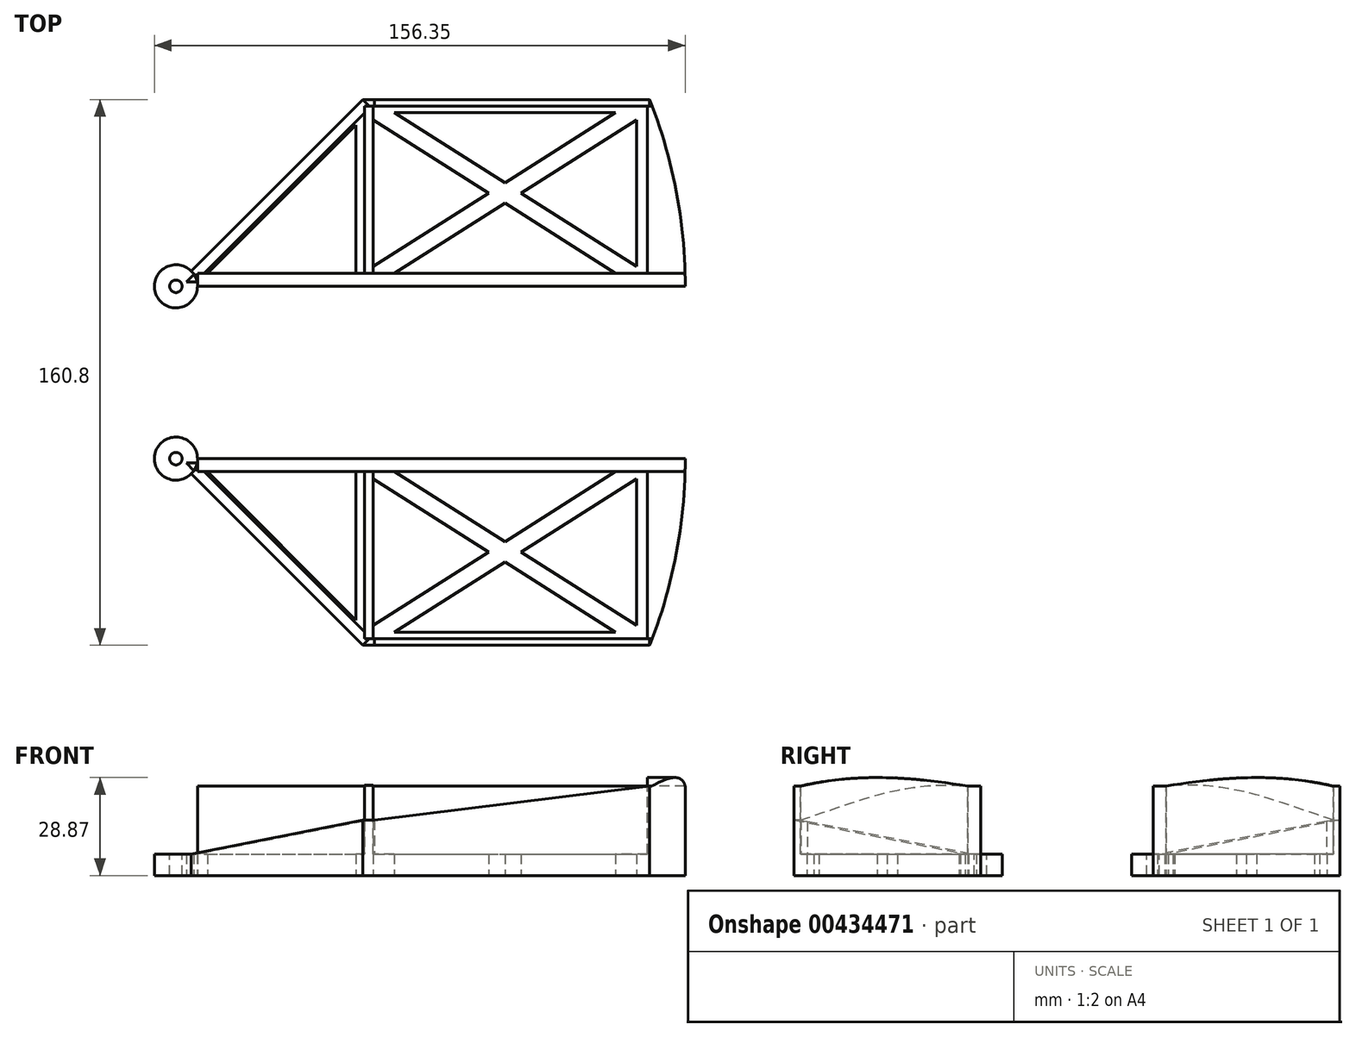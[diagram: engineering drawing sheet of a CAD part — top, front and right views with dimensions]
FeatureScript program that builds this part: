
annotation { "Feature Type Name" : "Feature", "Feature Type Description" : "" }
export const myFeature = defineFeature(function(context is Context, id is Id, definition is map)
    precondition{}
    {
        {
            var Q0;
            Q0=qCreatedBy(makeId("Top.planeOp"),FACE);
            var sketch = newSketch(context, id + "F0", { "sketchPlane" : qUnion([Q0]), "disableImprinting" : false});
            skLineSegment(sketch, "E0", {"start": v(0, 0) * mm, "end": v(55, 55) * mm});
            skLineSegment(sketch, "E1", {"start": v(55, 55) * mm, "end": v(139.55, 55) * mm});
            skLineSegment(sketch, "E2", {"start": v(139.55, 55) * mm, "end": v(139.55, 0) * mm});
            skLineSegment(sketch, "E3", {"start": v(139.55, 0) * mm, "end": v(0, 0) * mm});
            skLineSegment(sketch, "E4.0", {"start": v(3.14, 1.3) * mm, "end": v(55.54, 53.7) * mm});
            skLineSegment(sketch, "E4.1", {"start": v(138.25, 1.3) * mm, "end": v(3.14, 1.3) * mm});
            skLineSegment(sketch, "E4.2", {"start": v(138.25, 53.7) * mm, "end": v(138.25, 1.3) * mm});
            skLineSegment(sketch, "E4.3", {"start": v(55.54, 53.7) * mm, "end": v(138.25, 53.7) * mm});
            skLineSegment(sketch, "E5", {"start": v(55.54, 53.7) * mm, "end": v(96.9, 27.5) * mm});
            skLineSegment(sketch, "E6", {"start": v(55.54, 53.7) * mm, "end": v(55.54, 1.3) * mm});
            skLineSegment(sketch, "E7", {"start": v(96.9, 27.5) * mm, "end": v(138.25, 1.3) * mm});
            skLineSegment(sketch, "E8", {"start": v(55.54, 1.3) * mm, "end": v(96.9, 27.5) * mm});
            skLineSegment(sketch, "E9", {"start": v(96.9, 27.5) * mm, "end": v(138.25, 53.7) * mm});
            skLineSegment(sketch, "E10.0", {"start": v(58.08, 49.08) * mm, "end": v(58.08, 5.92) * mm});
            skLineSegment(sketch, "E10.1", {"start": v(58.08, 49.08) * mm, "end": v(92.15, 27.5) * mm});
            skLineSegment(sketch, "E10.2", {"start": v(58.08, 5.92) * mm, "end": v(92.15, 27.5) * mm});
            skLineSegment(sketch, "E11.0", {"start": v(64.3, 51.16) * mm, "end": v(96.9, 30.5) * mm});
            skLineSegment(sketch, "E11.1", {"start": v(64.3, 51.16) * mm, "end": v(129.5, 51.16) * mm});
            skLineSegment(sketch, "E11.2", {"start": v(96.9, 30.5) * mm, "end": v(129.5, 51.16) * mm});
            skLineSegment(sketch, "E12.0", {"start": v(101.64, 27.5) * mm, "end": v(135.71, 5.92) * mm});
            skLineSegment(sketch, "E12.1", {"start": v(101.64, 27.5) * mm, "end": v(135.71, 49.08) * mm});
            skLineSegment(sketch, "E12.2", {"start": v(135.71, 49.08) * mm, "end": v(135.71, 5.92) * mm});
            skLineSegment(sketch, "E13", {"start": v(64.3, 3.84) * mm, "end": v(96.9, 24.5) * mm});
            skLineSegment(sketch, "E14", {"start": v(96.9, 24.5) * mm, "end": v(129.5, 3.84) * mm});
            skLineSegment(sketch, "E15", {"start": v(129.5, 3.84) * mm, "end": v(64.3, 3.84) * mm});
            skLineSegment(sketch, "E16", {"start": v(9.27, 3.84) * mm, "end": v(53, 47.57) * mm});
            skLineSegment(sketch, "E17", {"start": v(53, 47.57) * mm, "end": v(53, 3.84) * mm});
            skLineSegment(sketch, "E18", {"start": v(53, 3.84) * mm, "end": v(9.27, 3.84) * mm});
            skCircle(sketch, "E19", {"center": v(0, 0) * mm, "radius": 6.35 * mm});
            skCircle(sketch, "E20", {"center": v(0, 0) * mm, "radius": 150 * mm});
            skLineSegment(sketch, "E21", {"start": v(139.55, 0) * mm, "end": v(150, 0) * mm});
            skSolve(sketch);
        }
        {
            var Q0;
            {var subQ0=sQuery(id+"F0.wireOp",EDGE,"E3");var subQ1=sQuery(id+"F0.wireOp",EDGE,"E0");var subQ2=makeQuery(id+"F0.imprint","INTERSECT",VERTEX,{"derivedFrom":[subQ1,subQ0]});Q0=makeQuery(id+"F0.imprint","IMPRINT",FACE,{"disambiguationData":[TD([[makeQuery(id+"F0.imprint","IMPRINT",EDGE,{"disambiguationData":[TD([[subQ2,-1.0]])],"derivedFrom":subQ1}),1.0]])]});}
            var Q1;
            {var subQ6=sQuery(id+"F0.wireOp",EDGE,"E3");var subQ7=sQuery(id+"F0.wireOp",EDGE,"E0");var subQ8=makeQuery(id+"F0.imprint","INTERSECT",VERTEX,{"derivedFrom":[subQ7,subQ6]});Q1=makeQuery(id+"F0.imprint","IMPRINT",FACE,{"disambiguationData":[TD([[makeQuery(id+"F0.imprint","IMPRINT",EDGE,{"disambiguationData":[TD([[subQ8,-1.0]])],"derivedFrom":subQ7}),-1.0]])]});}
            var Q2;
            {var subQ13=sQuery(id+"F0.wireOp",EDGE,"E1");Q2=makeQuery(id+"F0.imprint","IMPRINT",FACE,{"disambiguationData":[TD([[makeQuery(id+"F0.imprint","IMPRINT",EDGE,{"derivedFrom":subQ13}),-1.0]])]});}
            var Q3;
            {var subQ0=sQuery(id+"F0.wireOp",EDGE,"E6");Q3=makeQuery(id+"F0.imprint","IMPRINT",FACE,{"disambiguationData":[TD([[makeQuery(id+"F0.imprint","IMPRINT",EDGE,{"derivedFrom":subQ0}),-1.0]])]});}
            var Q4;
            Q4=makeQuery(id+"F0.imprint","IMPRINT",FACE,{"disambiguationData":[TD([[makeQuery(id+"F0.imprint","IMPRINT",EDGE,{"derivedFrom":sQuery(id+"F0.wireOp",EDGE,"E5")}),-1.0]])]});
            var Q5;
            {var subQ1=sQuery(id+"F0.wireOp",EDGE,"E7");Q5=makeQuery(id+"F0.imprint","IMPRINT",FACE,{"disambiguationData":[TD([[makeQuery(id+"F0.imprint","IMPRINT",EDGE,{"derivedFrom":subQ1}),-1.0]])]});}
            var Q6;
            Q6=makeQuery(id+"F0.imprint","IMPRINT",FACE,{"disambiguationData":[TD([[makeQuery(id+"F0.imprint","IMPRINT",EDGE,{"derivedFrom":sQuery(id+"F0.wireOp",EDGE,"E4.3")}),-1.0]])]});
            var Q7;
            Q7=makeQuery(id+"F0.imprint","IMPRINT",FACE,{"disambiguationData":[TD([[makeQuery(id+"F0.imprint","IMPRINT",EDGE,{"derivedFrom":sQuery(id+"F0.wireOp",EDGE,"E4.2")}),-1.0]])]});
            var Q8;
            {var subQ0=sQuery(id+"F0.wireOp",EDGE,"E2");Q8=makeQuery(id+"F0.imprint","IMPRINT",FACE,{"disambiguationData":[TD([[makeQuery(id+"F0.imprint","IMPRINT",EDGE,{"derivedFrom":subQ0}),1.0]])]});}
            extrude(context, id + "F1", {"entities" : qUnion([Q0, Q1, Q2, Q3, Q4, Q5, Q6, Q7, Q8]), "depth" : 6.35 * mm});
        }
        {
            var Q0;
            Q0=makeQuery(id+"F1.opExtrude","CAP_FACE",FACE,{"disambiguationData":[OSD([sQuery(id+"F0.wireOp",EDGE,"E0"),sQuery(id+"F0.wireOp",EDGE,"E1"),sQuery(id+"F0.wireOp",EDGE,"E2"),sQuery(id+"F0.wireOp",EDGE,"E3"),sQuery(id+"F0.wireOp",EDGE,"E10.0"),sQuery(id+"F0.wireOp",EDGE,"E10.1"),sQuery(id+"F0.wireOp",EDGE,"E10.2"),sQuery(id+"F0.wireOp",EDGE,"E11.0"),sQuery(id+"F0.wireOp",EDGE,"E11.1"),sQuery(id+"F0.wireOp",EDGE,"E11.2"),sQuery(id+"F0.wireOp",EDGE,"E12.0"),sQuery(id+"F0.wireOp",EDGE,"E12.1"),sQuery(id+"F0.wireOp",EDGE,"E12.2"),sQuery(id+"F0.wireOp",EDGE,"E13"),sQuery(id+"F0.wireOp",EDGE,"E14"),sQuery(id+"F0.wireOp",EDGE,"E15"),sQuery(id+"F0.wireOp",EDGE,"E16"),sQuery(id+"F0.wireOp",EDGE,"E17"),sQuery(id+"F0.wireOp",EDGE,"E18"),sQuery(id+"F0.wireOp",EDGE,"E19")])],"isStart":false});
            var sketch = newSketch(context, id + "F2", { "sketchPlane" : qUnion([Q0])});
            skCircle(sketch, "E22", {"center": v(0, 0) * mm, "radius": 1.84 * mm});
            skSolve(sketch);
        }
        {
            var Q0;
            Q0 = qSketchRegion(id + "F2", true);
            extrude(context, id + "F3", {"entities" : qUnion([Q0]), "operationType" : NewBodyOperationType.REMOVE, "oppositeDirection" : true, "depth" : 25.4 * mm});
        }
        {
            var Q0;
            Q0=makeQuery(id+"F1.opExtrude","CAP_FACE",FACE,{"disambiguationData":[OSD([sQuery(id+"F0.wireOp",EDGE,"E0"),sQuery(id+"F0.wireOp",EDGE,"E1"),sQuery(id+"F0.wireOp",EDGE,"E2"),sQuery(id+"F0.wireOp",EDGE,"E3"),sQuery(id+"F0.wireOp",EDGE,"E10.0"),sQuery(id+"F0.wireOp",EDGE,"E10.1"),sQuery(id+"F0.wireOp",EDGE,"E10.2"),sQuery(id+"F0.wireOp",EDGE,"E11.0"),sQuery(id+"F0.wireOp",EDGE,"E11.1"),sQuery(id+"F0.wireOp",EDGE,"E11.2"),sQuery(id+"F0.wireOp",EDGE,"E12.0"),sQuery(id+"F0.wireOp",EDGE,"E12.1"),sQuery(id+"F0.wireOp",EDGE,"E12.2"),sQuery(id+"F0.wireOp",EDGE,"E13"),sQuery(id+"F0.wireOp",EDGE,"E14"),sQuery(id+"F0.wireOp",EDGE,"E15"),sQuery(id+"F0.wireOp",EDGE,"E16"),sQuery(id+"F0.wireOp",EDGE,"E17"),sQuery(id+"F0.wireOp",EDGE,"E18"),sQuery(id+"F0.wireOp",EDGE,"E19")])],"isStart":false});
            var sketch = newSketch(context, id + "F4", { "sketchPlane" : qUnion([Q0])});
            skLineSegment(sketch, "E23.bottom", {"start": v(9.27, 0) * mm, "end": v(6.35, 0) * mm});
            skLineSegment(sketch, "E23.top", {"start": v(9.27, 3.84) * mm, "end": v(6.35, 3.84) * mm});
            skLineSegment(sketch, "E23.left", {"start": v(6.35, 0) * mm, "end": v(6.35, 3.84) * mm});
            skLineSegment(sketch, "E23.right", {"start": v(9.27, 0) * mm, "end": v(9.27, 3.84) * mm});
            skSolve(sketch);
        }
        {
            var Q0;
            Q0 = qSketchRegion(id + "F4", true);
            extrude(context, id + "F5", {"entities" : qUnion([Q0]), "operationType" : NewBodyOperationType.ADD, "depth" : 20 * mm});
        }
        {
            var Q0;
            Q0=makeQuery(id+"F1.opExtrude","SWEPT_FACE",FACE,{"disambiguationData":[OSD([sQuery(id+"F0.wireOp",EDGE,"E0")])]});
            var sketch = newSketch(context, id + "F6", { "sketchPlane" : qUnion([Q0])});
            skLineSegment(sketch, "E24", {"start": v(-77.78, 6.35) * mm, "end": v(-77.78, 16.35) * mm});
            skLineSegment(sketch, "E25", {"start": v(-77.78, 16.35) * mm, "end": v(-6.35, 6.35) * mm});
            skLineSegment(sketch, "E26", {"start": v(-6.35, 6.35) * mm, "end": v(-77.78, 6.35) * mm});
            skSolve(sketch);
        }
        {
            var Q0;
            Q0 = qSketchRegion(id + "F6", true);
            var Q1;
            Q1=makeQuery(id+"F1.opExtrude","SWEPT_FACE",FACE,{"disambiguationData":[OSD([sQuery(id+"F0.wireOp",EDGE,"E16")])]});
            extrude(context, id + "F7", {"entities" : qUnion([Q0]), "operationType" : NewBodyOperationType.ADD, "oppositeDirection" : true, "endBoundEntityFace" : qUnion([Q1]), "depth" : 3.17 * mm});
        }
        {
            var Q0;
            Q0=makeQuery(id+"F1.opExtrude","SWEPT_FACE",FACE,{"disambiguationData":[OSD([sQuery(id+"F0.wireOp",EDGE,"E1")])]});
            var sketch = newSketch(context, id + "F8", { "sketchPlane" : qUnion([Q0]), "disableImprinting" : false});
            skLineSegment(sketch, "E27", {"start": v(-139.55, 6.35) * mm, "end": v(-139.55, 26.35) * mm});
            skLineSegment(sketch, "E28", {"start": v(-139.55, 26.35) * mm, "end": v(-58.52, 16.35) * mm});
            skLineSegment(sketch, "E29", {"start": v(-58.52, 16.35) * mm, "end": v(-58.52, 6.35) * mm});
            skSolve(sketch);
        }
        {
            var Q0;
            {var subQ0=sQuery(id+"F8.wireOp",EDGE,"E27");Q0=makeQuery(id+"F8.imprint","IMPRINT",FACE,{"disambiguationData":[TD([[makeQuery(id+"F8.imprint","IMPRINT",EDGE,{"derivedFrom":subQ0}),-1.0]])]});}
            extrude(context, id + "F9", {"entities" : qUnion([Q0]), "operationType" : NewBodyOperationType.ADD, "oppositeDirection" : true, "depth" : 1.9 * mm});
        }
        {
            var Q1;
            Q1=makeQuery(id+"F7.opExtrude","SWEPT_FACE",FACE,{"disambiguationData":[OSD([sQuery(id+"F6.wireOp",EDGE,"E24")])]});
            var Q2;
            Q2=makeQuery(id+"F9.opExtrude","SWEPT_FACE",FACE,{"disambiguationData":[OSD([sQuery(id+"F8.wireOp",EDGE,"E29")])]});
            loft(context, id + "F10", {"operationType" : NewBodyOperationType.ADD, "sheetProfilesArray" : [{ "sheetProfileEntities" : qUnion([Q1]) }, { "sheetProfileEntities" : qUnion([Q2]) }]});
        }
        {
            var Q0;
            Q0=makeQuery(id+"F1.opExtrude","SWEPT_FACE",FACE,{"disambiguationData":[OSD([sQuery(id+"F0.wireOp",EDGE,"E10.0")])]});
            var sketch = newSketch(context, id + "F11", { "sketchPlane" : qUnion([Q0])});
            skLineSegment(sketch, "E30.0.0", {"start": v(0, 24.38) * mm, "end": v(0, 6.35) * mm});
            skFitSpline(sketch, "E30.0.1", {"points": [v(0, 24.38) * mm, v(1.99, 25.62) * mm, v(2.56, 26) * mm, v(3.84, 26.35) * mm]});
            skLineSegment(sketch, "E30.0.2", {"start": v(3.84, 6.35) * mm, "end": v(3.84, 26.35) * mm});
            skLineSegment(sketch, "E30.0.3", {"start": v(0, 6.35) * mm, "end": v(3.84, 6.35) * mm});
            skLineSegment(sketch, "E31.0.0", {"start": v(53.1, 21.18) * mm, "end": v(53.1, 26.35) * mm});
            skLineSegment(sketch, "E31.0.3", {"start": v(55, 16.35) * mm, "end": v(53.1, 16.35) * mm});
            skLineSegment(sketch, "E31.0.4", {"start": v(53.1, 16.35) * mm, "end": v(53.1, 21.18) * mm});
            skLineSegment(sketch, "E32", {"start": v(53.1, 16.35) * mm, "end": v(53.1, 6.35) * mm});
            skLineSegment(sketch, "E33", {"start": v(3.84, 6.35) * mm, "end": v(53.1, 6.35) * mm});
            skFitSpline(sketch, "E34", {"points": [v(53.1, 16.35) * mm, v(3.84, 26.35) * mm], "startDerivative": vector(-52.9, 16.95) * mm, "endDerivative": vector(-57.88, -5.03) * mm});
            skSolve(sketch);
        }
        {
            var Q0;
            {var subQ0=sQuery(id+"F11.wireOp",EDGE,"E32");Q0=makeQuery(id+"F11.imprint","IMPRINT",FACE,{"disambiguationData":[TD([[makeQuery(id+"F11.imprint","IMPRINT",EDGE,{"derivedFrom":subQ0}),-1.0]])]});}
            extrude(context, id + "F12", {"entities" : qUnion([Q0]), "operationType" : NewBodyOperationType.ADD, "oppositeDirection" : true, "depth" : 2.54 * mm});
        }
        {
            var Q0;
            Q0=makeQuery(id+"F5.boolean.opBoolean","MERGE",FACE,{"derivedFrom":[makeQuery(id+"F1.opExtrude","SWEPT_FACE",FACE,{"disambiguationData":[OSD([sQuery(id+"F0.wireOp",EDGE,"E3")])]}),makeQuery(id+"F5.opExtrude","SWEPT_FACE",FACE,{"disambiguationData":[OSD([sQuery(id+"F4.wireOp",EDGE,"E23.bottom")])]})]});
            cPlane(context, id + "F13", {"entities" : qUnion([Q0]), "cplaneType" : CPlaneType.OFFSET, "offset" : 25.4 * mm, "width" : 152.4 * mm, "height" : 152.4 * mm});
        }
        {
            var Q0;
            Q0=makeQuery(id+"F1.opExtrude","SWEPT_BODY",BODY,{"disambiguationData":[OSD([sQuery(id+"F0.wireOp",EDGE,"E0"),sQuery(id+"F0.wireOp",EDGE,"E1"),sQuery(id+"F0.wireOp",EDGE,"E2"),sQuery(id+"F0.wireOp",EDGE,"E3"),sQuery(id+"F0.wireOp",EDGE,"E10.0"),sQuery(id+"F0.wireOp",EDGE,"E10.1"),sQuery(id+"F0.wireOp",EDGE,"E10.2"),sQuery(id+"F0.wireOp",EDGE,"E11.0"),sQuery(id+"F0.wireOp",EDGE,"E11.1"),sQuery(id+"F0.wireOp",EDGE,"E11.2"),sQuery(id+"F0.wireOp",EDGE,"E12.0"),sQuery(id+"F0.wireOp",EDGE,"E12.1"),sQuery(id+"F0.wireOp",EDGE,"E12.2"),sQuery(id+"F0.wireOp",EDGE,"E13"),sQuery(id+"F0.wireOp",EDGE,"E14"),sQuery(id+"F0.wireOp",EDGE,"E15"),sQuery(id+"F0.wireOp",EDGE,"E16"),sQuery(id+"F0.wireOp",EDGE,"E17"),sQuery(id+"F0.wireOp",EDGE,"E18"),sQuery(id+"F0.wireOp",EDGE,"E19")])]});
            var Q1;
            Q1=qCreatedBy(id+"F13.planeOp",FACE);
            mirror(context, id + "F14", {"entities" : qUnion([Q0]), "mirrorPlane" : qUnion([Q1])});
        }
        {
            var Q0;
            Q0=makeQuery(id+"F5.opExtrude","SWEPT_FACE",FACE,{"disambiguationData":[OSD([sQuery(id+"F4.wireOp",EDGE,"E23.right")])]});
            var sketch = newSketch(context, id + "F15", { "sketchPlane" : qUnion([Q0])});
            skPoint(sketch, "E35.0", {"position": v(0, 26.35) * mm});
            skLineSegment(sketch, "E36.bottom", {"start": v(0, 26.35) * mm, "end": v(3.84, 26.35) * mm});
            skLineSegment(sketch, "E36.top", {"start": v(0, 6.35) * mm, "end": v(3.84, 6.35) * mm});
            skLineSegment(sketch, "E36.left", {"start": v(0, 26.35) * mm, "end": v(0, 6.35) * mm});
            skLineSegment(sketch, "E36.right", {"start": v(3.84, 26.35) * mm, "end": v(3.84, 6.35) * mm});
            skSolve(sketch);
        }
        {
            var Q0;
            Q0 = qSketchRegion(id + "F15", true);
            var Q1;
            Q1=makeQuery(id+"F1.opExtrude","SWEPT_FACE",FACE,{"disambiguationData":[OSD([sQuery(id+"F0.wireOp",EDGE,"E20")])]});
            extrude(context, id + "F16", {"entities" : qUnion([Q0]), "operationType" : NewBodyOperationType.ADD, "endBound" : BoundingType.UP_TO_SURFACE, "endBoundEntityFace" : qUnion([Q1]), "depth" : 25.4 * mm});
        }
        {
            var Q0;
            {var subQ0=sQuery(id+"F0.wireOp",EDGE,"E20");var subQ1=sQuery(id+"F0.wireOp",EDGE,"E18");var subQ2=sQuery(id+"F0.wireOp",EDGE,"E17");var subQ3=sQuery(id+"F0.wireOp",EDGE,"E16");var subQ4=sQuery(id+"F0.wireOp",EDGE,"E15");var subQ5=sQuery(id+"F0.wireOp",EDGE,"E14");var subQ6=sQuery(id+"F0.wireOp",EDGE,"E13");var subQ7=sQuery(id+"F0.wireOp",EDGE,"E12.2");var subQ8=sQuery(id+"F0.wireOp",EDGE,"E12.1");var subQ9=sQuery(id+"F0.wireOp",EDGE,"E10.0");var subQ10=sQuery(id+"F0.wireOp",EDGE,"E21");var subQ11=sQuery(id+"F0.wireOp",EDGE,"E3");var subQ12=sQuery(id+"F0.wireOp",EDGE,"E1");var subQ13=sQuery(id+"F0.wireOp",EDGE,"E0");var subQ14=sQuery(id+"F0.wireOp",EDGE,"E11.1");var subQ15=sQuery(id+"F0.wireOp",EDGE,"E10.1");var subQ16=sQuery(id+"F0.wireOp",EDGE,"E10.2");var subQ17=sQuery(id+"F0.wireOp",EDGE,"E11.0");var subQ18=sQuery(id+"F0.wireOp",EDGE,"E11.2");var subQ19=sQuery(id+"F0.wireOp",EDGE,"E12.0");Q0=makeQuery(id+"F14.opPattern","COPY",FACE,{"derivedFrom":makeQuery(id+"F7.boolean.opBoolean","SPLIT",FACE,{"disambiguationData":[TD([makeQuery(id+"F1.opExtrude","SWEPT_FACE",FACE,{"disambiguationData":[OSD([subQ12])]})])],"derivedFrom":makeQuery(id+"F1.opExtrude","CAP_FACE",FACE,{"disambiguationData":[OSD([subQ13,subQ12,subQ11,sQuery(id+"F0.wireOp",EDGE,"E4.0"),sQuery(id+"F0.wireOp",EDGE,"E4.1"),subQ9,subQ15,subQ16,subQ17,subQ14,subQ18,subQ19,subQ8,subQ7,subQ6,subQ5,subQ4,subQ3,subQ2,subQ1,sQuery(id+"F0.wireOp",EDGE,"E19"),subQ0,subQ10])],"isStart":false})}),"instanceName":"1"});}
            var sketch = newSketch(context, id + "F17", { "sketchPlane" : qUnion([Q0])});
            skLineSegment(sketch, "E37", {"start": v(139.55, -103.9) * mm, "end": v(140.29, -103.9) * mm});
            skLineSegment(sketch, "E38.0.0", {"start": v(58.08, -54.64) * mm, "end": v(58.08, -56.72) * mm});
            skLineSegment(sketch, "E38.0.1", {"start": v(58.08, -56.72) * mm, "end": v(92.15, -78.3) * mm});
            skLineSegment(sketch, "E38.0.2", {"start": v(92.15, -78.3) * mm, "end": v(58.08, -99.88) * mm});
            skLineSegment(sketch, "E38.0.3", {"start": v(58.08, -99.88) * mm, "end": v(58.08, -103.78) * mm});
            skLineSegment(sketch, "E38.0.4", {"start": v(58.08, -103.78) * mm, "end": v(58.52, -103.9) * mm});
            skLineSegment(sketch, "E38.0.5", {"start": v(58.52, -103.9) * mm, "end": v(139.55, -103.9) * mm});
            skLineSegment(sketch, "E38.0.6", {"start": v(139.55, -103.9) * mm, "end": v(139.55, -105.8) * mm});
            skArc(sketch, "E38.0.7", {"start": v(139.55, -105.8) * mm, "mid": v(147.37, -78.8) * mm, "end": v(150, -50.8) * mm});
            skLineSegment(sketch, "E38.0.8", {"start": v(150, -50.8) * mm, "end": v(9.27, -50.8) * mm});
            skLineSegment(sketch, "E38.0.9", {"start": v(9.27, -50.8) * mm, "end": v(9.27, -54.64) * mm});
            skLineSegment(sketch, "E38.0.10", {"start": v(9.27, -54.64) * mm, "end": v(53, -54.64) * mm});
            skLineSegment(sketch, "E38.0.11", {"start": v(53, -54.64) * mm, "end": v(53, -98.37) * mm});
            skLineSegment(sketch, "E38.0.12", {"start": v(53, -98.37) * mm, "end": v(9.27, -54.64) * mm});
            skLineSegment(sketch, "E38.0.13", {"start": v(9.27, -54.64) * mm, "end": v(8.33, -54.64) * mm});
            skLineSegment(sketch, "E38.0.14", {"start": v(8.33, -54.64) * mm, "end": v(55.54, -101.85) * mm});
            skLineSegment(sketch, "E38.0.15", {"start": v(55.54, -101.85) * mm, "end": v(55.54, -54.64) * mm});
            skLineSegment(sketch, "E38.0.16", {"start": v(55.54, -54.64) * mm, "end": v(58.08, -54.64) * mm});
            skSolve(sketch);
        }
        {
            var Q0;
            {var subQ0=sQuery(id+"F17.wireOp",EDGE,"E37");Q0=makeQuery(id+"F17.imprint","IMPRINT",FACE,{"disambiguationData":[TD([[makeQuery(id+"F17.imprint","IMPRINT",EDGE,{"derivedFrom":subQ0}),-1.0]])]});}
            var Q1;
            Q1=makeQuery(id+"F14.opPattern","COPY",VERTEX,{"derivedFrom":makeQuery(id+"F9.opExtrude","CAP_VERTEX",VERTEX,{"disambiguationData":[OSD([sQuery(id+"F8.wireOp",EDGE,"E27"),sQuery(id+"F8.wireOp",EDGE,"E28")])],"isStart":true}),"instanceName":"1"});
            extrude(context, id + "F18", {"entities" : qUnion([Q0]), "operationType" : NewBodyOperationType.ADD, "endBound" : BoundingType.UP_TO_VERTEX, "endBoundEntityVertex" : qUnion([Q1]), "depth" : 25.4 * mm});
        }
        {
            var Q0;
            Q0=makeQuery(id+"F14.opPattern","COPY",FACE,{"derivedFrom":makeQuery(id+"F1.opExtrude","SWEPT_FACE",FACE,{"disambiguationData":[OSD([sQuery(id+"F0.wireOp",EDGE,"E12.2")])]}),"instanceName":"1"});
            cPlane(context, id + "F19", {"entities" : qUnion([Q0]), "cplaneType" : CPlaneType.OFFSET, "offset" : 3.17 * mm, "oppositeDirection" : true, "width" : 152.4 * mm, "height" : 152.4 * mm});
        }
        {
            var Q0;
            Q0=qCreatedBy(id+"F19.planeOp",FACE);
            var sketch = newSketch(context, id + "F20", { "sketchPlane" : qUnion([Q0])});
            skLineSegment(sketch, "E39.0.0", {"start": v(105.8, 0) * mm, "end": v(50.8, 0) * mm});
            skLineSegment(sketch, "E39.0.1", {"start": v(50.8, 0) * mm, "end": v(50.8, 6.35) * mm});
            skLineSegment(sketch, "E39.0.2", {"start": v(50.8, 6.35) * mm, "end": v(103.9, 6.35) * mm});
            skLineSegment(sketch, "E39.0.3", {"start": v(103.9, 6.35) * mm, "end": v(103.9, 26.35) * mm});
            skLineSegment(sketch, "E39.0.4", {"start": v(103.9, 26.35) * mm, "end": v(105.8, 26.35) * mm});
            skLineSegment(sketch, "E39.0.5", {"start": v(105.8, 26.35) * mm, "end": v(105.8, 0) * mm});
            skLineSegment(sketch, "E40.0", {"start": v(54.64, 6.35) * mm, "end": v(54.64, 26.35) * mm});
            skFitSpline(sketch, "E41", {"points": [v(103.9, 26.35) * mm, v(54.64, 26.35) * mm], "startDerivative": vector(-47.91, 11.07) * mm, "endDerivative": vector(-54.43, -9.01) * mm});
            skSolve(sketch);
        }
        {
            var Q0;
            {var subQ0=sQuery(id+"F20.wireOp",EDGE,"E39.0.3");Q0=makeQuery(id+"F20.imprint","IMPRINT",FACE,{"disambiguationData":[TD([[makeQuery(id+"F20.imprint","IMPRINT",EDGE,{"derivedFrom":subQ0}),1.0]])]});}
            var Q1;
            Q1=makeQuery(id+"F18.boolean.opBoolean","MERGE",FACE,{"derivedFrom":[makeQuery(id+"F14.opPattern","COPY",FACE,{"derivedFrom":makeQuery(id+"F1.opExtrude","SWEPT_FACE",FACE,{"disambiguationData":[OSD([sQuery(id+"F0.wireOp",EDGE,"E20")])]}),"instanceName":"1"}),makeQuery(id+"F18.opExtrude","SWEPT_FACE",FACE,{"disambiguationData":[OSD([sQuery(id+"F17.wireOp",EDGE,"E38.0.7")])]})]});
            extrude(context, id + "F21", {"entities" : qUnion([Q0]), "operationType" : NewBodyOperationType.ADD, "endBound" : BoundingType.UP_TO_SURFACE, "oppositeDirection" : true, "endBoundEntityFace" : qUnion([Q1]), "depth" : 25.4 * mm});
        }
        {
            var Q0;
            Q0=makeQuery(id+"F14.opPattern","COPY",FACE,{"derivedFrom":makeQuery(id+"F5.opExtrude","SWEPT_FACE",FACE,{"disambiguationData":[OSD([sQuery(id+"F4.wireOp",EDGE,"E23.right")])]}),"instanceName":"1"});
            var sketch = newSketch(context, id + "F22", { "sketchPlane" : qUnion([Q0])});
            skLineSegment(sketch, "E42.bottom", {"start": v(-54.64, 26.35) * mm, "end": v(-50.8, 26.35) * mm});
            skLineSegment(sketch, "E42.top", {"start": v(-54.64, 6.35) * mm, "end": v(-50.8, 6.35) * mm});
            skLineSegment(sketch, "E42.left", {"start": v(-54.64, 26.35) * mm, "end": v(-54.64, 6.35) * mm});
            skLineSegment(sketch, "E42.right", {"start": v(-50.8, 26.35) * mm, "end": v(-50.8, 6.35) * mm});
            skSolve(sketch);
        }
        {
            var Q0;
            Q0 = qSketchRegion(id + "F22", true);
            var Q1;
            {var subQ0=sQuery(id+"F17.wireOp",EDGE,"E38.0.7");var subQ1=sQuery(id+"F0.wireOp",EDGE,"E20");Q1=makeQuery(id+"F21.boolean.opBoolean","MERGE",FACE,{"derivedFrom":[makeQuery(id+"F18.boolean.opBoolean","MERGE",FACE,{"derivedFrom":[makeQuery(id+"F14.opPattern","COPY",FACE,{"derivedFrom":makeQuery(id+"F1.opExtrude","SWEPT_FACE",FACE,{"disambiguationData":[OSD([subQ1])]}),"instanceName":"1"}),makeQuery(id+"F18.opExtrude","SWEPT_FACE",FACE,{"disambiguationData":[OSD([subQ0])]})]}),makeQuery(id+"F21.opExtrude","CAP_FACE",FACE,{"disambiguationData":[OSD([subQ1,subQ0])],"isStart":false})]});}
            extrude(context, id + "F23", {"entities" : qUnion([Q0]), "operationType" : NewBodyOperationType.ADD, "endBound" : BoundingType.UP_TO_SURFACE, "endBoundEntityFace" : qUnion([Q1]), "depth" : 25.4 * mm});
        }
        {
            var Q0;
            Q0=makeQuery(id+"F14.opPattern","COPY",BODY,{"derivedFrom":makeQuery(id+"F1.opExtrude","SWEPT_BODY",BODY,{"disambiguationData":[OSD([sQuery(id+"F0.wireOp",EDGE,"E0"),sQuery(id+"F0.wireOp",EDGE,"E1"),sQuery(id+"F0.wireOp",EDGE,"E3"),sQuery(id+"F0.wireOp",EDGE,"E4.0"),sQuery(id+"F0.wireOp",EDGE,"E4.1"),sQuery(id+"F0.wireOp",EDGE,"E10.0"),sQuery(id+"F0.wireOp",EDGE,"E10.1"),sQuery(id+"F0.wireOp",EDGE,"E10.2"),sQuery(id+"F0.wireOp",EDGE,"E11.0"),sQuery(id+"F0.wireOp",EDGE,"E11.1"),sQuery(id+"F0.wireOp",EDGE,"E11.2"),sQuery(id+"F0.wireOp",EDGE,"E12.0"),sQuery(id+"F0.wireOp",EDGE,"E12.1"),sQuery(id+"F0.wireOp",EDGE,"E12.2"),sQuery(id+"F0.wireOp",EDGE,"E13"),sQuery(id+"F0.wireOp",EDGE,"E14"),sQuery(id+"F0.wireOp",EDGE,"E15"),sQuery(id+"F0.wireOp",EDGE,"E16"),sQuery(id+"F0.wireOp",EDGE,"E17"),sQuery(id+"F0.wireOp",EDGE,"E18"),sQuery(id+"F0.wireOp",EDGE,"E19"),sQuery(id+"F0.wireOp",EDGE,"E20"),sQuery(id+"F0.wireOp",EDGE,"E21")])]}),"instanceName":"1"});
            var Q1;
            Q1=qCreatedBy(id+"F13.planeOp",FACE);
            mirror(context, id + "F24", {"operationType" : NewBodyOperationType.ADD, "entities" : qUnion([Q0]), "mirrorPlane" : qUnion([Q1])});
        }
    });
